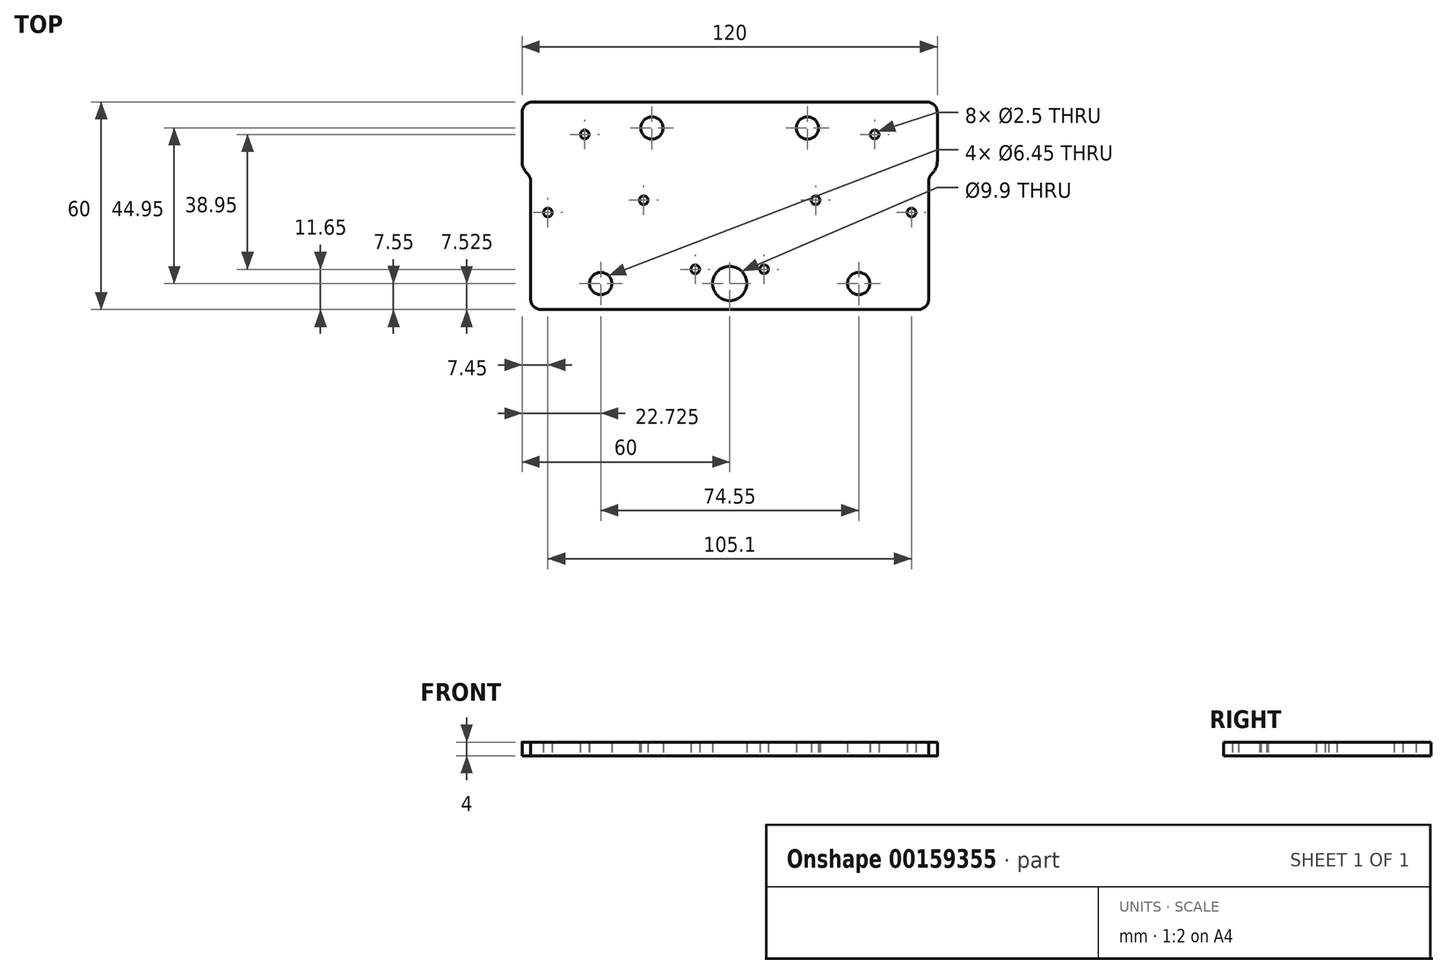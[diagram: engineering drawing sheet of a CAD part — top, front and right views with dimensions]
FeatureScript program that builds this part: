
annotation { "Feature Type Name" : "Feature", "Feature Type Description" : "" }
export const myFeature = defineFeature(function(context is Context, id is Id, definition is map)
    precondition{}
    {
        {
            var Q0;
            Q0=qCreatedBy(makeId("Top.planeOp"),FACE);
            var sketch = newSketch(context, id + "F0", { "sketchPlane" : qUnion([Q0])});
            skLineSegment(sketch, "E0.bottom", {"start": v(60, 30) * mm, "end": v(-60, 30) * mm});
            skLineSegment(sketch, "E0.top", {"start": v(60, -30) * mm, "end": v(-60, -30) * mm});
            skLineSegment(sketch, "E0.left", {"start": v(60, 30) * mm, "end": v(60, -30) * mm});
            skLineSegment(sketch, "E0.right", {"start": v(-60, 30) * mm, "end": v(-60, -30) * mm});
            skPoint(sketch, "E0.middle", {"position": v(0, 0) * mm});
            skPoint(sketch, "E1", {"position": v(-60, 10) * mm});
            skLineSegment(sketch, "E2", {"start": v(0, 30) * mm, "end": v(0, -30) * mm, "construction": true});
            skLineSegment(sketch, "E3", {"start": v(-60, 10) * mm, "end": v(-57.5, 10) * mm});
            skLineSegment(sketch, "E4", {"start": v(-57.5, 10) * mm, "end": v(-57.5, -30) * mm});
            skCircle(sketch, "E5", {"center": v(-41.9, 20.6) * mm, "radius": 1.25 * mm});
            skCircle(sketch, "E6", {"center": v(-52.55, -1.95) * mm, "radius": 1.25 * mm});
            skCircle(sketch, "E7", {"center": v(-24.85, 1.6) * mm, "radius": 1.25 * mm});
            skCircle(sketch, "E8", {"center": v(-22.48, 22.48) * mm, "radius": 3.23 * mm});
            skCircle(sketch, "E9", {"center": v(-37.27, -22.47) * mm, "radius": 3.23 * mm});
            skCircle(sketch, "E10", {"center": v(-9.95, -18.35) * mm, "radius": 1.25 * mm});
            skCircle(sketch, "E11", {"center": v(0, -22.45) * mm, "radius": 4.95 * mm});
            skCircle(sketch, "E12.MirrorC", {"center": v(22.48, 22.48) * mm, "radius": 3.23 * mm});
            skCircle(sketch, "E13.MirrorC", {"center": v(41.9, 20.6) * mm, "radius": 1.25 * mm});
            skCircle(sketch, "E14.MirrorC", {"center": v(24.85, 1.6) * mm, "radius": 1.25 * mm});
            skCircle(sketch, "E15.MirrorC", {"center": v(52.55, -1.95) * mm, "radius": 1.25 * mm});
            skCircle(sketch, "E16.MirrorC", {"center": v(9.95, -18.35) * mm, "radius": 1.25 * mm});
            skCircle(sketch, "E17.MirrorC", {"center": v(37.27, -22.47) * mm, "radius": 3.23 * mm});
            skLineSegment(sketch, "E18.MirrorCS", {"start": v(57.5, 10) * mm, "end": v(57.5, -30) * mm});
            skLineSegment(sketch, "E19.MirrorCS", {"start": v(60, 10) * mm, "end": v(57.5, 10) * mm});
            skSolve(sketch);
        }
        {
            var Q0;
            {var subQ1=sQuery(id+"F0.wireOp",EDGE,"E0.bottom");Q0=makeQuery(id+"F0.imprint","IMPRINT",FACE,{"disambiguationData":[TD([[makeQuery(id+"F0.imprint","IMPRINT",EDGE,{"derivedFrom":subQ1}),1.0]])]});}
            extrude(context, id + "F1", {"entities" : qUnion([Q0]), "depth" : 4 * mm});
        }
        {
            var Q0;
            Q0=makeQuery(id+"F1.opExtrude","SWEPT_EDGE",EDGE,{"disambiguationData":[OSD([sQuery(id+"F0.wireOp",EDGE,"E3"),sQuery(id+"F0.wireOp",EDGE,"E4")])]});
            var Q1;
            Q1=makeQuery(id+"F1.opExtrude","SWEPT_EDGE",EDGE,{"disambiguationData":[OSD([sQuery(id+"F0.wireOp",EDGE,"E18.MirrorCS"),sQuery(id+"F0.wireOp",EDGE,"E19.MirrorCS")])]});
            var Q2;
            Q2=makeQuery(id+"F1.opExtrude","SWEPT_EDGE",EDGE,{"disambiguationData":[OSD([sQuery(id+"F0.wireOp",EDGE,"E0.bottom"),sQuery(id+"F0.wireOp",EDGE,"E0.left")])]});
            var Q3;
            Q3=makeQuery(id+"F1.opExtrude","SWEPT_EDGE",EDGE,{"disambiguationData":[OSD([sQuery(id+"F0.wireOp",EDGE,"E0.bottom"),sQuery(id+"F0.wireOp",EDGE,"E0.right")])]});
            var Q4;
            Q4=makeQuery(id+"F1.opExtrude","SWEPT_EDGE",EDGE,{"disambiguationData":[OSD([sQuery(id+"F0.wireOp",EDGE,"E0.top"),sQuery(id+"F0.wireOp",EDGE,"E4")])]});
            var Q5;
            Q5=makeQuery(id+"F1.opExtrude","SWEPT_EDGE",EDGE,{"disambiguationData":[OSD([sQuery(id+"F0.wireOp",EDGE,"E0.top"),sQuery(id+"F0.wireOp",EDGE,"E18.MirrorCS")])]});
            fillet(context, id + "F2", {"entities" : qUnion([Q0, Q1, Q2, Q3, Q4, Q5]), "radius" : 3 * mm, "tangentPropagation" : true, "allowEdgeOverflow" : false});
        }
        {
            var Q0;
            Q0=makeQuery(id+"F2.opFillet","BLEND_EDGE",EDGE,{"blendedFrom":[makeQuery(id+"F1.opExtrude","SWEPT_EDGE",EDGE,{"disambiguationData":[OSD([sQuery(id+"F0.wireOp",EDGE,"E3"),sQuery(id+"F0.wireOp",EDGE,"E4")])]}),makeQuery(id+"F1.opExtrude","SWEPT_FACE",FACE,{"disambiguationData":[OSD([sQuery(id+"F0.wireOp",EDGE,"E0.right")])]})],"blendedInto":[makeQuery(id+"F1.opExtrude","SWEPT_FACE",FACE,{"disambiguationData":[OSD([sQuery(id+"F0.wireOp",EDGE,"E0.right")])]})]});
            var Q1;
            Q1=makeQuery(id+"F2.opFillet","BLEND_EDGE",EDGE,{"blendedFrom":[makeQuery(id+"F1.opExtrude","SWEPT_EDGE",EDGE,{"disambiguationData":[OSD([sQuery(id+"F0.wireOp",EDGE,"E18.MirrorCS"),sQuery(id+"F0.wireOp",EDGE,"E19.MirrorCS")])]}),makeQuery(id+"F1.opExtrude","SWEPT_FACE",FACE,{"disambiguationData":[OSD([sQuery(id+"F0.wireOp",EDGE,"E0.left")])]})],"blendedInto":[makeQuery(id+"F1.opExtrude","SWEPT_FACE",FACE,{"disambiguationData":[OSD([sQuery(id+"F0.wireOp",EDGE,"E0.left")])]})]});
            fillet(context, id + "F3", {"entities" : qUnion([Q0, Q1]), "radius" : 5 * mm, "tangentPropagation" : true, "allowEdgeOverflow" : false});
        }
    });
